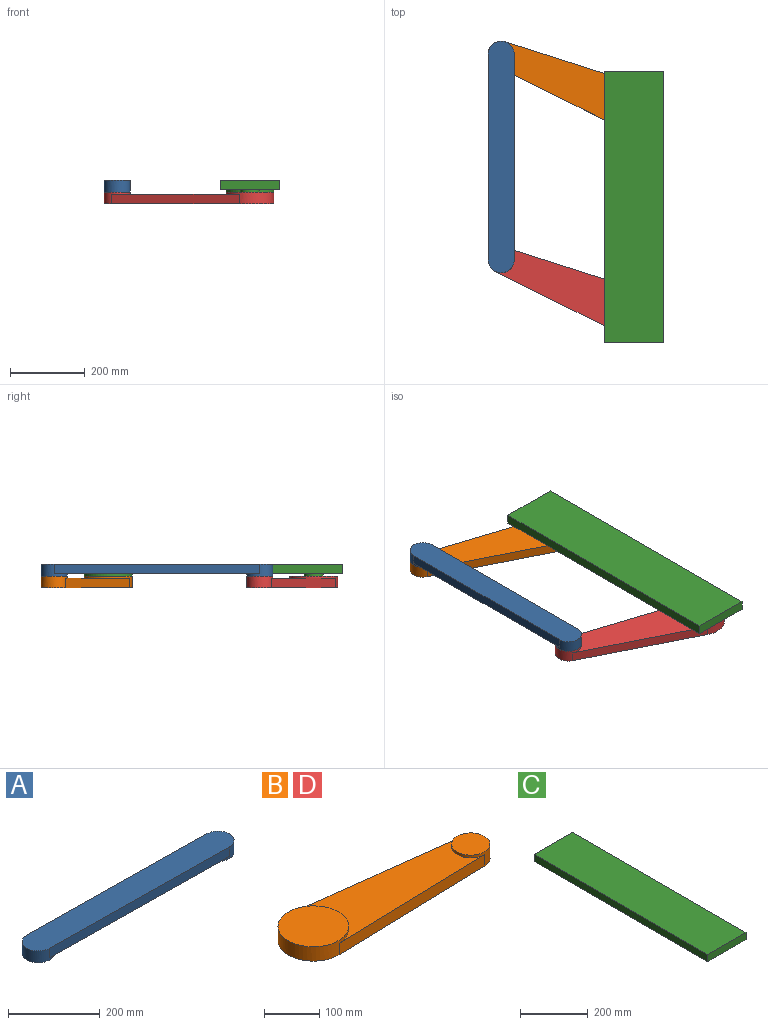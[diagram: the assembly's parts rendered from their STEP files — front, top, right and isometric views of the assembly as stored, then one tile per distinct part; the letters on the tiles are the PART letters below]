
ASSEMBLY  parts=4 mates=4
PART A: 8 faces, bbox 619.1x76.3x31.8 mm
  f0: cylinder r=34.74mm len=69.48mm, axis (0,0,-1), area 4158.4mm2, adj f1,f3,f4,f5,f6
  f1: plane 549.61x25.4mm, normal (-0.01,-1,0), area 13961.1mm2, adj f0,f2,f4,f5
  f2: cylinder r=34.74mm len=69.48mm, axis (0,0,-1), area 4158.4mm2, adj f1,f3,f4,f5,f7
  f3: plane 549.61x25.4mm, normal (0.01,1,0), area 13961.1mm2, adj f0,f2,f4,f5
  f4: plane 619.09x76.33mm, normal (0,0,1), area 41983.1mm2, adj f0,f1,f2,f3
  f5: plane 550.47x76.33mm, normal (0,0,-1), area 34399.5mm2, adj f0,f1,f2,f3
  f6: plane 69.48x69.48mm, normal (0,0,-1), area 3791.8mm2, adj f0
  f7: plane 69.48x69.48mm, normal (0,0,-1), area 3791.8mm2, adj f2
PART B: 8 faces, bbox 481.1x127.6x31.8 mm
  f0: plane 385.15x127.1mm, normal (0,0,1), area 29559.6mm2, adj f1,f2,f3,f4
  f1: plane 378.87x47.74mm, normal (0.13,0.99,0), area 9699.4mm2, adj f0,f2,f4,f5
  f2: cylinder r=63.81mm len=127.62mm, axis (0,0,-1), area 7884.1mm2, adj f0,f1,f3,f5,f6
  f3: plane 381.73x25.4mm, normal (0.03,-1,0), area 9699.4mm2, adj f0,f2,f4,f5
  f4: cylinder r=34.74mm len=69.48mm, axis (0,0,-1), area 4024.3mm2, adj f0,f1,f3,f5,f7
  f5: plane 481.06x127.62mm, normal (0,0,-1), area 46143.5mm2, adj f1,f2,f3,f4
  f6: plane 127.62x127.62mm, normal (0,0,1), area 12792.1mm2, adj f2
  f7: plane 69.48x69.48mm, normal (0,0,1), area 3791.8mm2, adj f4
PART C: 10 faces, bbox 159.4x725.3x31.8 mm
  f0: plane 159.42x25.4mm, normal (0,-1,0), area 4049.2mm2, adj f1,f3,f4,f5
  f1: plane 725.32x25.4mm, normal (1,0,0), area 18423.2mm2, adj f0,f2,f4,f5
  f2: plane 159.42x25.4mm, normal (0,1,0), area 4049.2mm2, adj f1,f3,f4,f5
  f3: plane 725.32x25.4mm, normal (-1,0,0), area 18423.2mm2, adj f0,f2,f4,f5
  f4: plane 725.32x159.42mm, normal (0,0,-1), area 100811.3mm2, adj f0,f1,f2,f3,f6,f8
  f5: plane 725.32x159.42mm, normal (0,0,1), area 115630.2mm2, adj f0,f1,f2,f3
  f6: cylinder r=63.81mm len=127.62mm, axis (0,0,1), area 2545.9mm2, adj f4,f7
  f7: plane 127.62x127.62mm, normal (0,0,-1), area 12792.1mm2, adj f6
  f8: cylinder r=25.4mm len=50.8mm, axis (0,0,1), area 1013.4mm2, adj f4,f9
  f9: plane 50.8x50.8mm, normal (0,0,-1), area 2026.8mm2, adj f8
PART D: same geometry as B
PLACE A rot(axis=(0,0,1),90.7deg) t=(-160.87,-201.58,-6.82)mm
PLACE B rot(axis=(0,0,1),160.7deg) t=(-29.14,253.19,-44.92)mm
PLACE C t=(-579.79,-51.74,18.58)mm fixed
PLACE D rot(axis=(0,0,1),160.7deg) t=(-29.14,-296.42,-44.92)mm
MATE revolute A.f2 <-> B.f4  axis (0,0,-1) through (-348.29,382.81,-13.17)mm
MATE revolute C.f6 <-> B.f2  axis (0,0,-1) through (6.5,238.62,-13.17)mm
MATE revolute D.f2 <-> C.f8  axis (0,0,1) through (6.5,-310.98,-13.17)mm
MATE revolute A.f0 <-> D.f4  axis (0,0,-1) through (-348.31,-166.84,-13.17)mm
